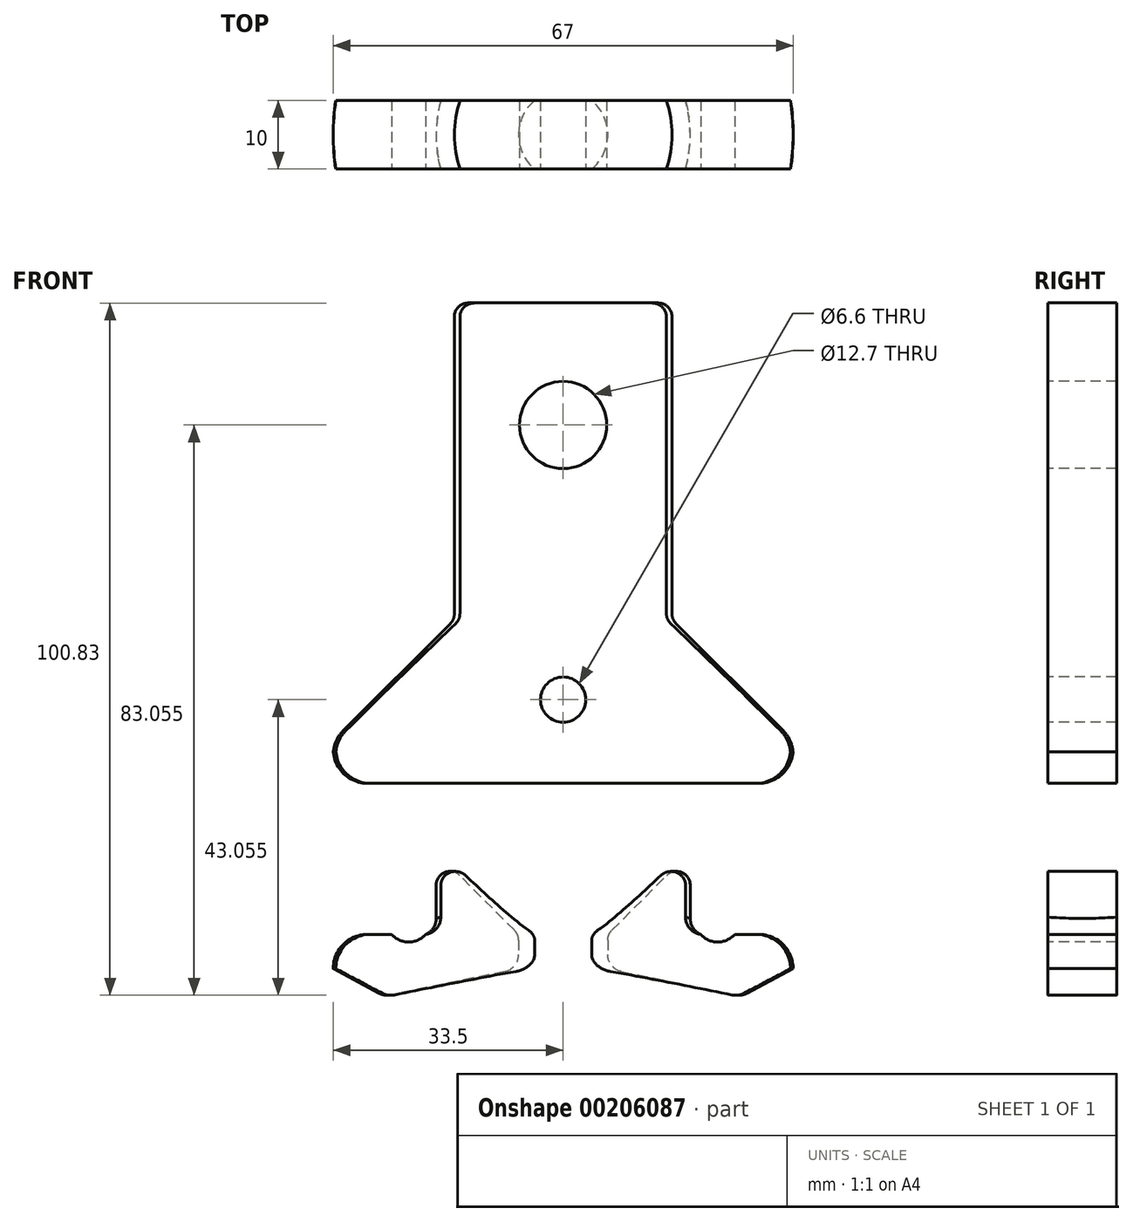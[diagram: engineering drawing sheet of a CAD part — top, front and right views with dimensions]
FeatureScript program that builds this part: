
annotation { "Feature Type Name" : "Feature", "Feature Type Description" : "" }
export const myFeature = defineFeature(function(context is Context, id is Id, definition is map)
    precondition{}
    {
        {
            var Q0;
            Q0=qCreatedBy(makeId("Front.planeOp"),FACE);
            var sketch = newSketch(context, id + "F0", { "sketchPlane" : qUnion([Q0])});
            skLineSegment(sketch, "E0", {"start": v(6.5, 0) * mm, "end": v(18.5, 12) * mm});
            skLineSegment(sketch, "E1", {"start": v(18.5, 12) * mm, "end": v(18.5, 22) * mm});
            skLineSegment(sketch, "E2", {"start": v(18.5, 22) * mm, "end": v(0, 22) * mm});
            skLineSegment(sketch, "E3", {"start": v(6.5, 0) * mm, "end": v(33.5, 0) * mm});
            skLineSegment(sketch, "E4", {"start": v(33.5, 0) * mm, "end": v(33.5, 28.21) * mm});
            skLineSegment(sketch, "E5", {"start": v(15.85, 91.96) * mm, "end": v(0, 91.96) * mm});
            skLineSegment(sketch, "E6", {"start": v(0, 91.96) * mm, "end": v(0, 22) * mm});
            skCircle(sketch, "E7", {"center": v(0, 74.18) * mm, "radius": 6.35 * mm});
            skPoint(sketch, "E8", {"position": v(0, 80.53) * mm});
            skLineSegment(sketch, "E9.bottom", {"start": v(18.5, 22) * mm, "end": v(-18.5, 22) * mm});
            skLineSegment(sketch, "E9.top", {"start": v(18.5, 0) * mm, "end": v(-18.5, 0) * mm});
            skLineSegment(sketch, "E9.left", {"start": v(18.5, 22) * mm, "end": v(18.5, 0) * mm});
            skLineSegment(sketch, "E9.right", {"start": v(-18.5, 22) * mm, "end": v(-18.5, 0) * mm});
            skLineSegment(sketch, "E10", {"start": v(15.85, 91.96) * mm, "end": v(15.85, 45.86) * mm});
            skLineSegment(sketch, "E11", {"start": v(15.85, 45.86) * mm, "end": v(33.5, 28.21) * mm});
            skLineSegment(sketch, "E12", {"start": v(6.5, 0) * mm, "end": v(6.5, -5) * mm});
            skLineSegment(sketch, "E13", {"start": v(6.5, -5) * mm, "end": v(33.5, -5) * mm});
            skLineSegment(sketch, "E14", {"start": v(33.5, -5) * mm, "end": v(33.5, 0) * mm});
            skLineSegment(sketch, "E15", {"start": v(6.5, -5) * mm, "end": v(26, -9) * mm});
            skLineSegment(sketch, "E16", {"start": v(26, -9) * mm, "end": v(33.5, -5) * mm});
            skLineSegment(sketch, "E17", {"start": v(18.5, 22) * mm, "end": v(29.1, 32.6) * mm, "construction": true});
            skLineSegment(sketch, "E18", {"start": v(18.5, 22) * mm, "end": v(33.5, 22) * mm});
            skSolve(sketch);
        }
        {
            var Q0;
            {var subQ0=sQuery(id+"F0.wireOp",EDGE,"E7");var subQ1=sQuery(id+"F0.wireOp",EDGE,"E6");var subQ2=makeQuery(id+"F0.imprint","INTERSECT",VERTEX,{"disambiguationData":[OD(0.0)],"derivedFrom":[subQ1,subQ0]});Q0=makeQuery(id+"F0.imprint","IMPRINT",FACE,{"disambiguationData":[TD([[makeQuery(id+"F0.imprint","IMPRINT",EDGE,{"disambiguationData":[TD([[subQ2,-1.0]])],"derivedFrom":subQ1}),1.0]])]});}
            var Q1;
            {var subQ10=sQuery(id+"F0.wireOp",EDGE,"E3");Q1=makeQuery(id+"F0.imprint","IMPRINT",FACE,{"disambiguationData":[TD([[makeQuery(id+"F0.imprint","IMPRINT",EDGE,{"derivedFrom":subQ10}),1.0]])]});}
            var Q2;
            {var subQ0=sQuery(id+"F0.wireOp",EDGE,"E0");Q2=makeQuery(id+"F0.imprint","IMPRINT",FACE,{"disambiguationData":[TD([[makeQuery(id+"F0.imprint","IMPRINT",EDGE,{"derivedFrom":subQ0}),-1.0]])]});}
            var Q3;
            {var subQ2=sQuery(id+"F0.wireOp",EDGE,"E3");Q3=makeQuery(id+"F0.imprint","IMPRINT",FACE,{"disambiguationData":[TD([[makeQuery(id+"F0.imprint","IMPRINT",EDGE,{"derivedFrom":subQ2}),-1.0]])]});}
            var Q4;
            Q4=makeQuery(id+"F0.imprint","IMPRINT",FACE,{"disambiguationData":[TD([[makeQuery(id+"F0.imprint","IMPRINT",EDGE,{"derivedFrom":sQuery(id+"F0.wireOp",EDGE,"E13")}),-1.0]])]});
            var Q5;
            {var subQ9=sQuery(id+"F0.wireOp",EDGE,"E5");Q5=makeQuery(id+"F0.imprint","IMPRINT",FACE,{"disambiguationData":[TD([[makeQuery(id+"F0.imprint","IMPRINT",EDGE,{"derivedFrom":subQ9}),1.0]])]});}
            var Q6;
            Q6=sQuery(id+"F0.wireOp",EDGE,"E6");
            revolve(context, id + "F1", {"entities" : qUnion([Q0, Q1, Q2, Q3, Q4, Q5]), "axis" : qUnion([Q6]), "revolveType" : RevolveType.ONE_DIRECTION, "oppositeDirection" : true, "angle" : 360 * degree});
        }
        {
            var Q0;
            Q0=makeQuery(id+"F1.opRevolve","SWEPT_FACE",FACE,{"disambiguationData":[OSD([sQuery(id+"F0.wireOp",EDGE,"E5")])]});
            var sketch = newSketch(context, id + "F2", { "sketchPlane" : qUnion([Q0])});
            skLineSegment(sketch, "E19.bottom", {"start": v(-33.5, 33.5) * mm, "end": v(33.5, 33.5) * mm});
            skLineSegment(sketch, "E19.top", {"start": v(-33.5, 5) * mm, "end": v(33.5, 5) * mm});
            skLineSegment(sketch, "E19.left", {"start": v(-33.5, 33.5) * mm, "end": v(-33.5, 5) * mm});
            skLineSegment(sketch, "E19.right", {"start": v(33.5, 33.5) * mm, "end": v(33.5, 5) * mm});
            skLineSegment(sketch, "E20.bottom", {"start": v(-33.5, -33.5) * mm, "end": v(33.5, -33.5) * mm});
            skLineSegment(sketch, "E20.top", {"start": v(-33.5, -5) * mm, "end": v(33.5, -5) * mm});
            skLineSegment(sketch, "E20.left", {"start": v(-33.5, -33.5) * mm, "end": v(-33.5, -5) * mm});
            skLineSegment(sketch, "E20.right", {"start": v(33.5, -33.5) * mm, "end": v(33.5, -5) * mm});
            skLineSegment(sketch, "E21", {"start": v(0, 5) * mm, "end": v(0, -5) * mm, "construction": true});
            skSolve(sketch);
        }
        {
            var Q0;
            Q0=makeQuery(id+"F2.imprint","IMPRINT",FACE,{"disambiguationData":[TD([[makeQuery(id+"F2.imprint","IMPRINT",EDGE,{"derivedFrom":sQuery(id+"F2.wireOp",EDGE,"E20.bottom")}),1.0]])]});
            var Q1;
            Q1=makeQuery(id+"F2.imprint","IMPRINT",FACE,{"disambiguationData":[TD([[makeQuery(id+"F2.imprint","IMPRINT",EDGE,{"derivedFrom":sQuery(id+"F2.wireOp",EDGE,"E19.bottom")}),-1.0]])]});
            var Q2;
            {var subQ0=sQuery(id+"F2.wireOp",EDGE,"E20.top");var subQ1=makeQuery(id+"F1.opRevolve","SWEPT_EDGE",EDGE,{"disambiguationData":[OSD([sQuery(id+"F0.wireOp",EDGE,"E5"),sQuery(id+"F0.wireOp",EDGE,"E10")])]});var subQ2=makeQuery(id+"F2.imprint","INTERSECT",VERTEX,{"disambiguationData":[OD(0.0)],"derivedFrom":[subQ1,subQ0]});Q2=makeQuery(id+"F2.imprint","IMPRINT",FACE,{"disambiguationData":[TD([[makeQuery(id+"F2.imprint","IMPRINT",EDGE,{"disambiguationData":[TD([[subQ2,-1.0]])],"derivedFrom":subQ0}),-1.0]])]});}
            var Q3;
            {var subQ0=sQuery(id+"F2.wireOp",EDGE,"E19.top");var subQ1=makeQuery(id+"F1.opRevolve","SWEPT_EDGE",EDGE,{"disambiguationData":[OSD([sQuery(id+"F0.wireOp",EDGE,"E5"),sQuery(id+"F0.wireOp",EDGE,"E10")])]});var subQ2=makeQuery(id+"F2.imprint","INTERSECT",VERTEX,{"disambiguationData":[OD(0.0)],"derivedFrom":[subQ1,subQ0]});Q3=makeQuery(id+"F2.imprint","IMPRINT",FACE,{"disambiguationData":[TD([[makeQuery(id+"F2.imprint","IMPRINT",EDGE,{"disambiguationData":[TD([[subQ2,-1.0]])],"derivedFrom":subQ0}),1.0]])]});}
            extrude(context, id + "F3", {"entities" : qUnion([Q0, Q1, Q2, Q3]), "operationType" : NewBodyOperationType.REMOVE, "endBound" : BoundingType.THROUGH_ALL, "oppositeDirection" : true, "depth" : 25 * mm});
        }
        {
            var Q0;
            Q0=makeQuery(id+"F1.opRevolve","SWEPT_EDGE",EDGE,{"disambiguationData":[OSD([sQuery(id+"F0.wireOp",EDGE,"FI2kWnsq-bYjR-toCD-jMWB-uaBhb8gfH4dN"),sQuery(id+"F0.wireOp",EDGE,"DZJPYPuS-xWPI-OwPd-xfq3-0R899iDrHJfV")])]});
            var Q1;
            Q1=makeQuery(id+"F1.opRevolve","SWEPT_EDGE",EDGE,{"disambiguationData":[OSD([sQuery(id+"F0.wireOp",EDGE,"DZJPYPuS-xWPI-OwPd-xfq3-0R899iDrHJfV"),sQuery(id+"F0.wireOp",EDGE,"E5")])]});
            var Q2;
            Q2=makeQuery(id+"F1.opRevolve","SWEPT_EDGE",EDGE,{"disambiguationData":[OSD([sQuery(id+"F0.wireOp",EDGE,"E0"),sQuery(id+"F0.wireOp",EDGE,"E9.top")])]});
            var Q3;
            Q3=makeQuery(id+"F1.opRevolve","SWEPT_EDGE",EDGE,{"disambiguationData":[OSD([sQuery(id+"F0.wireOp",EDGE,"E0"),sQuery(id+"F0.wireOp",EDGE,"E9.left")])]});
            var Q4;
            Q4=makeQuery(id+"F1.opRevolve","SWEPT_EDGE",EDGE,{"disambiguationData":[OSD([sQuery(id+"F0.wireOp",EDGE,"E10"),sQuery(id+"F0.wireOp",EDGE,"E11")])]});
            fillet(context, id + "F4", {"entities" : qUnion([Q0, Q1, Q2, Q3, Q4]), "radius" : 2 * mm, "tangentPropagation" : true, "allowEdgeOverflow" : false});
        }
        {
            var Q0;
            Q0=qCreatedBy(makeId("Front.planeOp"),FACE);
            var sketch = newSketch(context, id + "F5", { "sketchPlane" : qUnion([Q0])});
            skCircle(sketch, "E22", {"center": v(0, 74.18) * mm, "radius": 6.35 * mm});
            skCircle(sketch, "E23", {"center": v(22.5, 2.18) * mm, "radius": 3.3 * mm});
            skCircle(sketch, "E24", {"center": v(0, 34.18) * mm, "radius": 3.3 * mm});
            skCircle(sketch, "E25", {"center": v(-22.5, 2.18) * mm, "radius": 3.3 * mm});
            skLineSegment(sketch, "E26", {"start": v(22.5, 2.18) * mm, "end": v(-22.5, 2.18) * mm, "construction": true});
            skPoint(sketch, "E27", {"position": v(0, 2.18) * mm});
            skPoint(sketch, "E27.positionSnap0", {"position": v(0, 2.18) * mm});
            skSolve(sketch);
        }
        {
            var Q0;
            Q0 = qSketchRegion(id + "F5", true);
            extrude(context, id + "F6", {"entities" : qUnion([Q0]), "operationType" : NewBodyOperationType.REMOVE, "endBound" : BoundingType.THROUGH_ALL, "oppositeDirection" : true, "depth" : 25 * mm, "hasSecondDirection" : true, "secondDirectionBound" : SecondDirectionBoundingType.THROUGH_ALL, "secondDirectionOppositeDirection" : false, "secondDirectionDepth" : 25 * mm});
        }
        {
            var Q0;
            Q0=makeQuery(id+"F1.opRevolve","SWEPT_EDGE",EDGE,{"disambiguationData":[OSD([sQuery(id+"F0.wireOp",EDGE,"E4"),sQuery(id+"F0.wireOp",EDGE,"FI2kWnsq-bYjR-toCD-jMWB-uaBhb8gfH4dN")])]});
            var Q1;
            Q1=makeQuery(id+"F1.opRevolve","SWEPT_EDGE",EDGE,{"disambiguationData":[OSD([sQuery(id+"F0.wireOp",EDGE,"E3"),sQuery(id+"F0.wireOp",EDGE,"E4")])]});
            fillet(context, id + "F7", {"entities" : qUnion([Q0, Q1]), "radius" : 5 * mm, "tangentPropagation" : true, "allowEdgeOverflow" : false});
        }
        {
            var Q0;
            Q0=makeQuery(id+"F1.opRevolve","SWEPT_EDGE",EDGE,{"disambiguationData":[OSD([sQuery(id+"F0.wireOp",EDGE,"E9.bottom"),sQuery(id+"F0.wireOp",EDGE,"E9.left")])]});
            var Q1;
            Q1=makeQuery(id+"F1uewWIMPZ3ajT9_1.boolean.opBoolean","COPY",EDGE,{"derivedFrom":makeQuery(id+"F1uewWIMPZ3ajT9_1.opExtrude","CAP_EDGE",EDGE,{"disambiguationData":[OSD([sQuery(id+"F5.wireOp",EDGE,"9wDBNp5m-kJux-o5BL-9qMn-IMAsFSHTvKGn")])],"isStart":true})});
            var Q2;
            Q2=makeQuery(id+"F1uewWIMPZ3ajT9_1.boolean.opBoolean","COPY",EDGE,{"derivedFrom":makeQuery(id+"F1uewWIMPZ3ajT9_1.opExtrude","SWEPT_EDGE",EDGE,{"disambiguationData":[OSD([sQuery(id+"F5.wireOp",EDGE,"mV04Bt11-Ou6Z-f7Wr-9GvA-9ZIzNDh8KCzS"),sQuery(id+"F5.wireOp",EDGE,"9wDBNp5m-kJux-o5BL-9qMn-IMAsFSHTvKGn")])]})});
            var Q3;
            Q3=makeQuery(id+"Fr8qs1tSwam8Usj_1.1.F1uewWIMPZ3ajT9_1.boolean.opBoolean","COPY",EDGE,{"derivedFrom":makeQuery(id+"Fr8qs1tSwam8Usj_1.1.F1uewWIMPZ3ajT9_1.opExtrude","CAP_EDGE",EDGE,{"disambiguationData":[OSD([sQuery(id+"F5.wireOp",EDGE,"9wDBNp5m-kJux-o5BL-9qMn-IMAsFSHTvKGn")])],"isStart":true})});
            var Q4;
            Q4=makeQuery(id+"F1.opRevolve","SWEPT_EDGE",EDGE,{"disambiguationData":[OSD([sQuery(id+"F0.wireOp",EDGE,"E12"),sQuery(id+"F0.wireOp",EDGE,"E13")])]});
            var Q5;
            Q5=makeQuery(id+"F1.opRevolve","SWEPT_EDGE",EDGE,{"disambiguationData":[OSD([sQuery(id+"F0.wireOp",EDGE,"E15"),sQuery(id+"F0.wireOp",EDGE,"E16")])]});
            var Q6;
            {var subQ0=sQuery(id+"F0.wireOp",EDGE,"E14");var subQ1=sQuery(id+"F0.wireOp",EDGE,"E16");var subQ2=sQuery(id+"F5.wireOp",EDGE,"PkLVZlg5-R7hm-ZfW5-ujiu-X7ZrtIV1N4OI");Q6=makeQuery(id+"Fr8qs1tSwam8Usj_1.1.F1uewWIMPZ3ajT9_1.boolean.opBoolean","SPLIT",EDGE,{"disambiguationData":[TD([makeQuery(id+"F1uewWIMPZ3ajT9_1.boolean.opBoolean","COPY",FACE,{"derivedFrom":makeQuery(id+"F1uewWIMPZ3ajT9_1.opExtrude","SWEPT_FACE",FACE,{"disambiguationData":[OSD([subQ2])]})})])],"derivedFrom":makeQuery(id+"F1uewWIMPZ3ajT9_1.boolean.opBoolean","SPLIT",EDGE,{"disambiguationData":[OD(1.0)],"derivedFrom":makeQuery(id+"F1.opRevolve","SWEPT_EDGE",EDGE,{"disambiguationData":[OSD([sQuery(id+"F0.wireOp",EDGE,"E13"),subQ0,subQ1])]})})});}
            fillet(context, id + "F8", {"entities" : qUnion([Q0, Q1, Q2, Q3, Q4, Q5, Q6]), "radius" : 2.5 * mm, "tangentPropagation" : true, "allowEdgeOverflow" : false});
        }
    });
